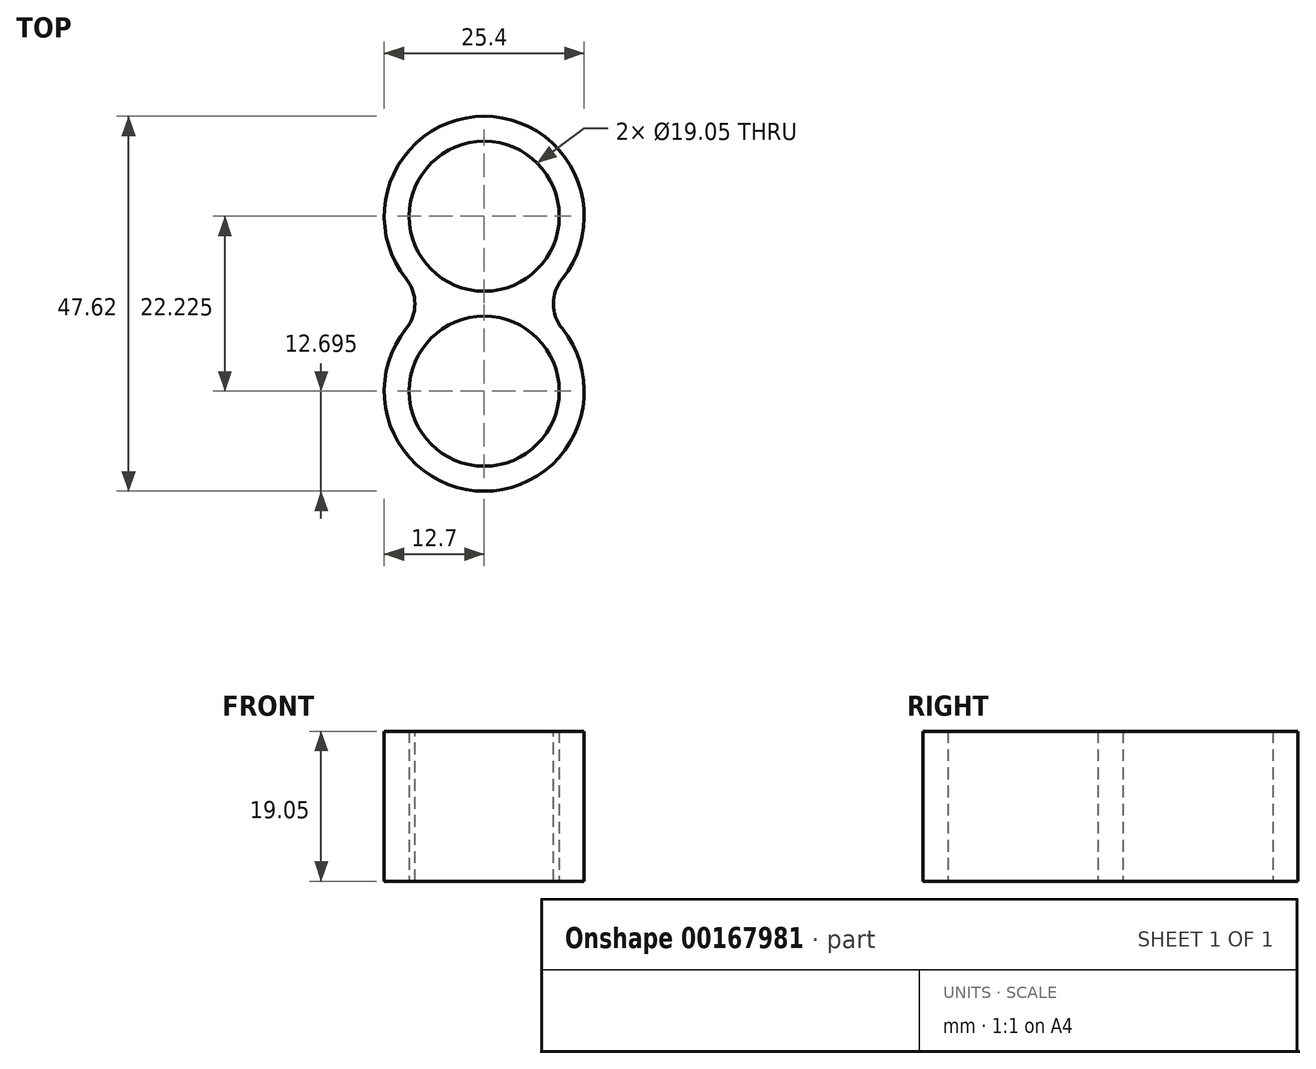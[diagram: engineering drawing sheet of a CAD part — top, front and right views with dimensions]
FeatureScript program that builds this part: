
annotation { "Feature Type Name" : "Feature", "Feature Type Description" : "" }
export const myFeature = defineFeature(function(context is Context, id is Id, definition is map)
    precondition{}
    {
        {
            var Q0;
            Q0=qCreatedBy(makeId("Top.planeOp"),FACE);
            var sketch = newSketch(context, id + "F0", { "sketchPlane" : qUnion([Q0])});
            skCircle(sketch, "E0", {"center": v(0, 0) * mm, "radius": 9.53 * mm});
            skArc(sketch, "E1.0", {"start": v(6.15, -11.11) * mm, "mid": v(0, 12.7) * mm, "end": v(-6.15, -11.11) * mm});
            skCircle(sketch, "E2", {"center": v(0, -22.23) * mm, "radius": 9.53 * mm});
            skArc(sketch, "E3.0", {"start": v(-6.15, -11.11) * mm, "mid": v(0, -34.92) * mm, "end": v(6.15, -11.11) * mm});
            skSolve(sketch);
        }
        {
            var Q0;
            Q0 = qSketchRegion(id + "F0", true);
            extrude(context, id + "F1", {"entities" : qUnion([Q0]), "depth" : 19.05 * mm});
        }
        {
            var Q0;
            {var subQ0=sQuery(id+"F0.wireOp",EDGE,"E3.0");var subQ1=sQuery(id+"F0.wireOp",EDGE,"E1.0");Q0=makeQuery(id+"F1.opExtrude","SWEPT_EDGE",EDGE,{"disambiguationData":[OSD([subQ1,subQ0]),TDD([makeQuery(id+"F0.imprint","INTERSECT",VERTEX,{"disambiguationData":[OD(0.0)],"derivedFrom":[subQ1,subQ0]})])]});}
            var Q1;
            {var subQ0=sQuery(id+"F0.wireOp",EDGE,"E3.0");var subQ1=sQuery(id+"F0.wireOp",EDGE,"E1.0");Q1=makeQuery(id+"F1.opExtrude","SWEPT_EDGE",EDGE,{"disambiguationData":[OSD([subQ1,subQ0]),TDD([makeQuery(id+"F0.imprint","INTERSECT",VERTEX,{"disambiguationData":[OD(1.0)],"derivedFrom":[subQ1,subQ0]})])]});}
            fillet(context, id + "F2", {"entities" : qUnion([Q0, Q1]), "radius" : 5.08 * mm, "tangentPropagation" : true, "allowEdgeOverflow" : false});
        }
    });
